# Revit family: БВО_RV17_LOD400 (04.11.23)
name_source: partatom
category: Электрооборудование
revit_build: Autodesk Revit 2017 (Build: 20170118_1100(x64)
units: mm (PartAtom-declared; Revit-internal decimal feet)

## family parameters
Всегда вертикально = Да
Конфигурация панели = Два столбца, слева направо
На основе рабочей плоскости = Нет
Общий = Нет
При загрузке вырезать с полостями = Нет
Размер круглого соединителя = Использовать диаметр
Тип детали = Щит
Точка расчета площади = Нет

## types (1)
- БВО
    ADSK_URL страницы изделия = https://stilsoft.ru
    ADSK_Единица измерения = шт.
    ADSK_Завод-изготовитель = ООО «Основа Безопасности»
    ADSK_Количество = 1
    ADSK_Марка = СТАЕ.426471.200
    ADSK_Масса = 1.4
    ADSK_Наименование = Блок ввода оптической линии БВО
    ADSK_Размер_Высота = 40 мм
    ADSK_Размер_Глубина = 145 мм
    ADSK_Размер_Длина = 294 мм
    d_короба = 20 мм
    Диапазон рабочих температур, <unrecoverable-encoding: 5 bytes ef82b0d0a1> = от –40 до +50
    Количество вводов оптического кабеля = 2
    Количество выходных разъёмов = 4
    Конфигурация выходных разъёмов = 2xLC
    Тип соединяемого волокна = Одномодовое
